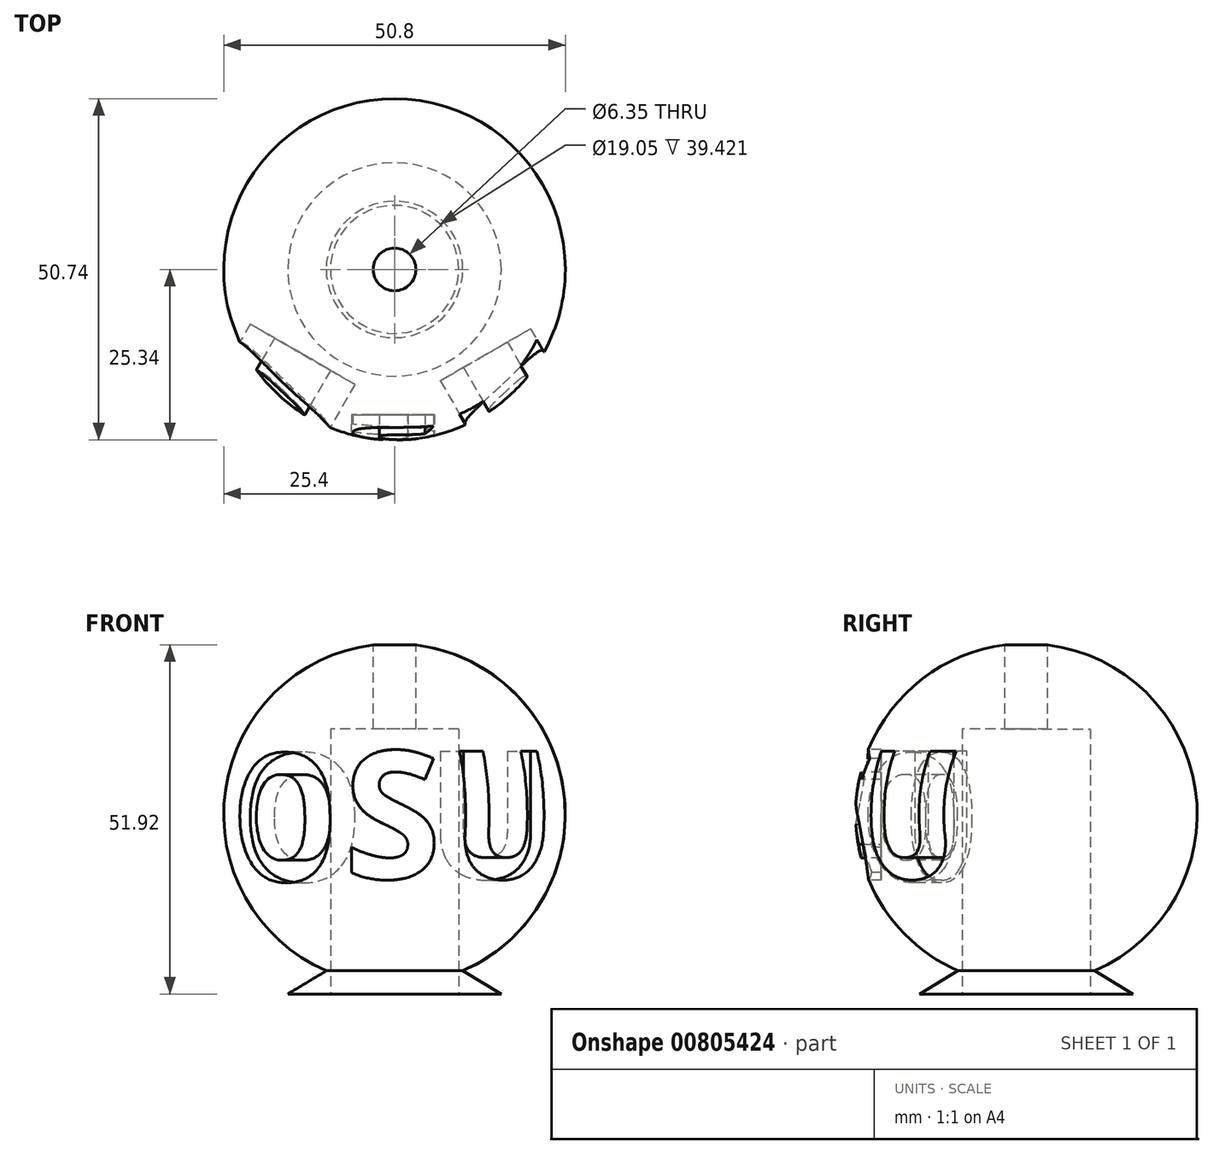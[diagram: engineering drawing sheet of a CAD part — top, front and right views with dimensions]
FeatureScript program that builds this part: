
annotation { "Feature Type Name" : "Feature", "Feature Type Description" : "" }
export const myFeature = defineFeature(function(context is Context, id is Id, definition is map)
    precondition{}
    {
        {
            var Q0;
            Q0=qCreatedBy(makeId("Front.planeOp"),FACE);
            var sketch = newSketch(context, id + "F0", { "sketchPlane" : qUnion([Q0])});
            skArc(sketch, "E0", {"start": v(0, 25.4) * mm, "mid": v(-25.4, 0) * mm, "end": v(0, -25.4) * mm});
            skLineSegment(sketch, "E1", {"start": v(0, 25.4) * mm, "end": v(0, -25.4) * mm});
            skSolve(sketch);
        }
        {
            var Q0;
            Q0=makeQuery(id+"F0.imprint","IMPRINT",FACE,{"disambiguationData":[TD([[makeQuery(id+"F0.imprint","IMPRINT",EDGE,{"derivedFrom":sQuery(id+"F0.wireOp",EDGE,"E0")}),1.0]])]});
            var Q1;
            Q1=sQuery(id+"F0.wireOp",EDGE,"E1");
            revolve(context, id + "F1", {"surfaceOperationType" : NewSurfaceOperationType.NEW, "entities" : qUnion([Q0]), "axis" : qUnion([Q1]), "revolveType" : RevolveType.FULL});
        }
        {
            var Q0;
            Q0=qCreatedBy(makeId("Top.planeOp"),FACE);
            var sketch = newSketch(context, id + "F2", { "sketchPlane" : qUnion([Q0])});
            skCircle(sketch, "E2", {"center": v(0, 0) * mm, "radius": 3.18 * mm});
            skSolve(sketch);
        }
        {
            var Q0;
            Q0 = qSketchRegion(id + "F2", true);
            extrude(context, id + "F3", {"entities" : qUnion([Q0]), "operationType" : NewBodyOperationType.REMOVE, "endBound" : BoundingType.SYMMETRIC, "oppositeDirection" : true, "depth" : 101.6 * mm, "offsetDistance" : 25.4 * mm});
        }
        {
            var Q0;
            Q0=qCreatedBy(makeId("Front.planeOp"),FACE);
            cPlane(context, id + "F4", {"entities" : qUnion([Q0]), "cplaneType" : CPlaneType.OFFSET, "offset" : 31.75 * mm, "width" : 152.4 * mm, "height" : 152.4 * mm});
        }
        {
            var Q0;
            Q0=qCreatedBy(makeId("Top.planeOp"),FACE);
            var sketch = newSketch(context, id + "F5", { "sketchPlane" : qUnion([Q0])});
            skLineSegment(sketch, "E3", {"start": v(0, 0) * mm, "end": v(0, -38.1) * mm});
            skLineSegment(sketch, "E4", {"start": v(0, -38.1) * mm, "end": v(35.62, -17.53) * mm});
            skLineSegment(sketch, "E5", {"start": v(0, -38.1) * mm, "end": v(-36.14, -17.24) * mm});
            skSolve(sketch);
        }
        {
            var Q0;
            Q0=sQuery(id+"F5.wireOp",EDGE,"E5");
            var Q1;
            Q1=qCreatedBy(id+"F4.planeOp",FACE);
            cPlane(context, id + "F6", {"entities" : qUnion([Q0, Q1]), "cplaneType" : CPlaneType.LINE_ANGLE, "offset" : 25.4 * mm, "angle" : 0 * degree, "width" : 152.4 * mm, "height" : 152.4 * mm});
        }
        {
            var Q0;
            Q0=sQuery(id+"F5.wireOp",EDGE,"E4");
            var Q1;
            Q1=qCreatedBy(id+"F4.planeOp",FACE);
            cPlane(context, id + "F7", {"entities" : qUnion([Q0, Q1]), "cplaneType" : CPlaneType.LINE_ANGLE, "offset" : 25.4 * mm, "angle" : 0 * degree, "width" : 152.4 * mm, "height" : 152.4 * mm});
        }
        {
            var Q0;
            Q0=qCreatedBy(id+"F4.planeOp",FACE);
            var sketch = newSketch(context, id + "F8", { "sketchPlane" : qUnion([Q0])});
            skText(sketch, "E6", { "text": "S", "fontName": "OpenSans-Bold.ttf"});
            const initialGuessF8  = {"E6": [-0.00762, -0.00953, 1, 0, 0.01905]};
            skSetInitialGuess(sketch, initialGuessF8);
            skSolve(sketch);
        }
        {
            var Q0;
            Q0=qCreatedBy(id+"F6.planeOp",FACE);
            var sketch = newSketch(context, id + "F9", { "sketchPlane" : qUnion([Q0])});
            skText(sketch, "E7", { "text": "O", "fontName": "OpenSans-Bold.ttf"});
            const initialGuessF9  = {"E7": [-0.005, -0.00993, 1, 0, 0.01905]};
            skSetInitialGuess(sketch, initialGuessF9);
            skSolve(sketch);
        }
        {
            var Q0;
            Q0=qCreatedBy(id+"F7.planeOp",FACE);
            var sketch = newSketch(context, id + "F10", { "sketchPlane" : qUnion([Q0])});
            skText(sketch, "E8", { "text": "U", "fontName": "OpenSans-Bold.ttf"});
            const initialGuessF10  = {"E8": [-0.01536, -0.00953, 1, 0, 0.01905]};
            skSetInitialGuess(sketch, initialGuessF10);
            skSolve(sketch);
        }
        {
            var Q0;
            Q0 = qSketchRegion(id + "F8", true);
            extrude(context, id + "F11", {"entities" : qUnion([Q0]), "operationType" : NewBodyOperationType.REMOVE, "oppositeDirection" : true, "depth" : 10.16 * mm, "offsetDistance" : 25.4 * mm});
        }
        {
            var Q0;
            Q0 = qSketchRegion(id + "F9", true);
            extrude(context, id + "F12", {"entities" : qUnion([Q0]), "operationType" : NewBodyOperationType.REMOVE, "depth" : 15.24 * mm, "offsetDistance" : 25.4 * mm});
        }
        {
            var Q0;
            Q0 = qSketchRegion(id + "F10", true);
            extrude(context, id + "F13", {"entities" : qUnion([Q0]), "operationType" : NewBodyOperationType.REMOVE, "depth" : 15.24 * mm, "offsetDistance" : 25.4 * mm});
        }
        {
            var Q0;
            Q0=qCreatedBy(makeId("Top.planeOp"),FACE);
            cPlane(context, id + "F14", {"entities" : qUnion([Q0]), "cplaneType" : CPlaneType.OFFSET, "offset" : 25.4 * mm, "oppositeDirection" : true, "width" : 152.4 * mm, "height" : 152.4 * mm});
        }
        {
            var Q0;
            Q0=qCreatedBy(makeId("Front.planeOp"),FACE);
            var sketch = newSketch(context, id + "F15", { "sketchPlane" : qUnion([Q0])});
            skLineSegment(sketch, "E9", {"start": v(0, 0) * mm, "end": v(0, 38.1) * mm});
            skSolve(sketch);
        }
        {
            var Q0;
            Q0=qCreatedBy(id+"F14.planeOp",FACE);
            var sketch = newSketch(context, id + "F16", { "sketchPlane" : qUnion([Q0])});
            skCircle(sketch, "E10", {"center": v(0, 0) * mm, "radius": 9.53 * mm});
            skSolve(sketch);
        }
        {
            var Q0;
            Q0 = qSketchRegion(id + "F16", true);
            extrude(context, id + "F17", {"entities" : qUnion([Q0]), "operationType" : NewBodyOperationType.REMOVE, "depth" : 38.1 * mm, "offsetDistance" : 25.4 * mm});
        }
        {
            var Q0;
            Q0=qCreatedBy(makeId("Front.planeOp"),FACE);
            var sketch = newSketch(context, id + "F18", { "sketchPlane" : qUnion([Q0])});
            skLineSegment(sketch, "E11", {"start": v(-10.08, -23.24) * mm, "end": v(-15.87, -26.72) * mm});
            skLineSegment(sketch, "E12", {"start": v(-15.87, -26.72) * mm, "end": v(-9.52, -26.72) * mm});
            skLineSegment(sketch, "E13", {"start": v(-9.52, -26.72) * mm, "end": v(-9.52, -23.55) * mm});
            skLineSegment(sketch, "E14", {"start": v(-9.52, -23.55) * mm, "end": v(-10.08, -23.24) * mm});
            skSolve(sketch);
        }
        {
            var Q0;
            Q0 = qSketchRegion(id + "F18", true);
            var Q1;
            Q1=sQuery(id+"F15.wireOp",EDGE,"E9");
            revolve(context, id + "F19", {"operationType" : NewBodyOperationType.ADD, "surfaceOperationType" : NewSurfaceOperationType.NEW, "entities" : qUnion([Q0]), "axis" : qUnion([Q1]), "revolveType" : RevolveType.FULL});
        }
    });
